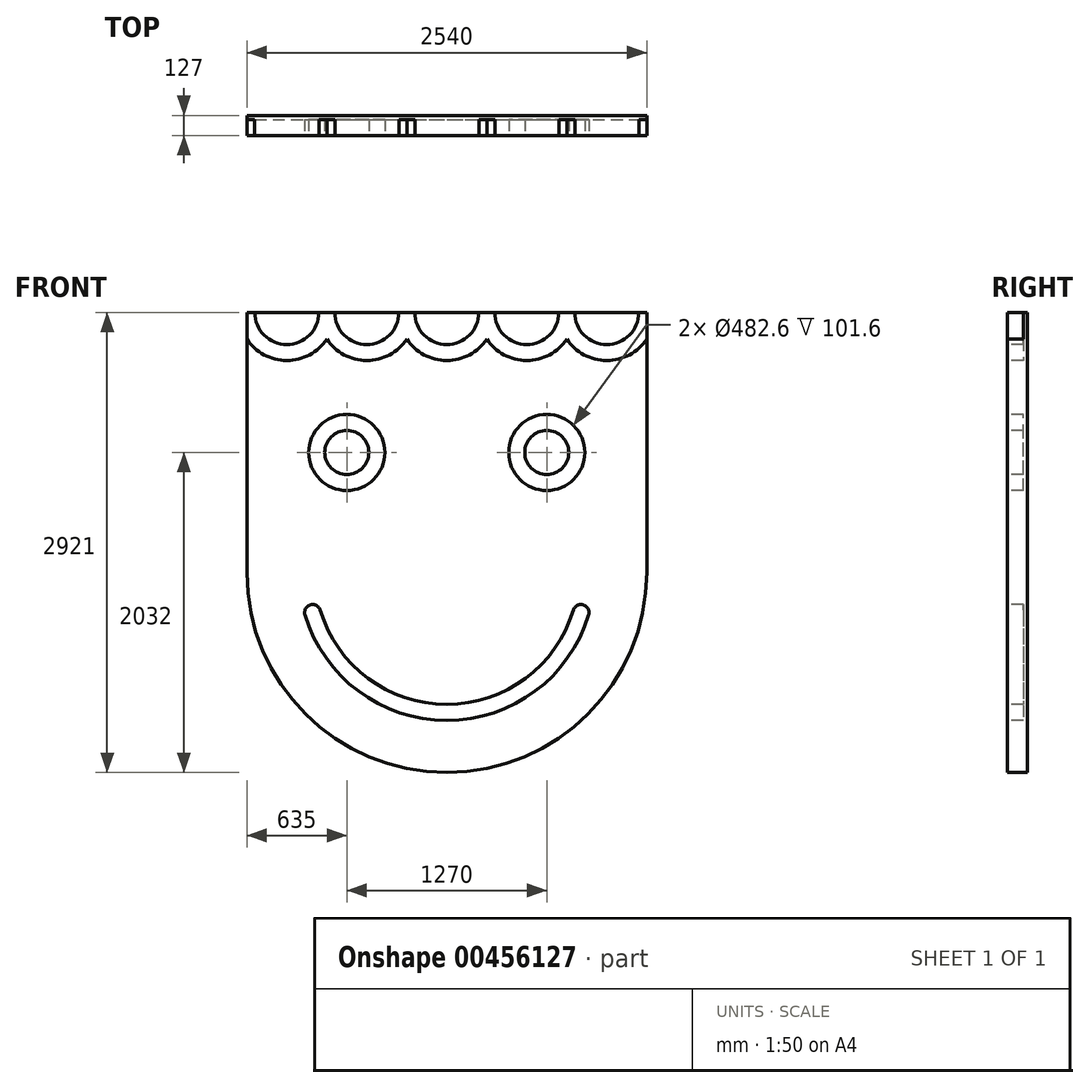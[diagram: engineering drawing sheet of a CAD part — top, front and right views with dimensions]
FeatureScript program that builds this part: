
annotation { "Feature Type Name" : "Feature", "Feature Type Description" : "" }
export const myFeature = defineFeature(function(context is Context, id is Id, definition is map)
    precondition{}
    {
        {
            var Q0;
            Q0=qCreatedBy(makeId("Front.planeOp"),FACE);
            var sketch = newSketch(context, id + "F0", { "sketchPlane" : qUnion([Q0])});
            skArc(sketch, "E0", {"start": v(-1270, 0) * mm, "mid": v(0, -1270) * mm, "end": v(1270, 0) * mm});
            skLineSegment(sketch, "E1", {"start": v(-1270, 0) * mm, "end": v(-1270, 1651) * mm});
            skLineSegment(sketch, "E2", {"start": v(-1270, 1651) * mm, "end": v(1270, 1651) * mm});
            skLineSegment(sketch, "E3", {"start": v(1270, 1651) * mm, "end": v(1270, 0) * mm});
            skSolve(sketch);
        }
        {
            var Q0;
            Q0 = qSketchRegion(id + "F0", true);
            extrude(context, id + "F1", {"entities" : qUnion([Q0]), "depth" : 127 * mm});
        }
        {
            var Q0;
            Q0=makeQuery(id+"F1.opExtrude","CAP_FACE",FACE,{"disambiguationData":[OSD([sQuery(id+"F0.wireOp",EDGE,"E0"),sQuery(id+"F0.wireOp",EDGE,"E1"),sQuery(id+"F0.wireOp",EDGE,"E2"),sQuery(id+"F0.wireOp",EDGE,"E3")])],"isStart":false});
            var sketch = newSketch(context, id + "F2", { "sketchPlane" : qUnion([Q0])});
            skArc(sketch, "E4", {"start": v(-851.94, -254) * mm, "mid": v(0, -889) * mm, "end": v(851.94, -254) * mm, "construction": true});
            skLineSegment(sketch, "E5", {"start": v(-1346.86, 0) * mm, "end": v(1410.17, 0) * mm, "construction": true});
            skCircle(sketch, "E6", {"center": v(-635, 762) * mm, "radius": 190.5 * mm, "construction": true});
            skCircle(sketch, "E7", {"center": v(635, 762) * mm, "radius": 190.5 * mm, "construction": true});
            skLineSegment(sketch, "E8", {"start": v(0, 0) * mm, "end": v(0, 1870.82) * mm, "construction": true});
            skArc(sketch, "E9", {"start": v(-1270, 1651) * mm, "mid": v(-1016, 1397) * mm, "end": v(-762, 1651) * mm, "construction": true});
            skArc(sketch, "E10", {"start": v(-762, 1651) * mm, "mid": v(-508, 1397) * mm, "end": v(-254, 1651) * mm, "construction": true});
            skArc(sketch, "E11", {"start": v(-254, 1651) * mm, "mid": v(0, 1397) * mm, "end": v(254, 1651) * mm, "construction": true});
            skArc(sketch, "E12", {"start": v(254, 1651) * mm, "mid": v(508, 1397) * mm, "end": v(762, 1651) * mm, "construction": true});
            skArc(sketch, "E13", {"start": v(762, 1651) * mm, "mid": v(1016, 1397) * mm, "end": v(1270, 1651) * mm, "construction": true});
            skArc(sketch, "E14.0.startCap", {"start": v(-1320.8, 1651) * mm, "mid": v(-1270, 1701.8) * mm, "end": v(-1219.2, 1651) * mm});
            skArc(sketch, "E14.0.endCap", {"start": v(-812.8, 1651) * mm, "mid": v(-762, 1701.8) * mm, "end": v(-711.2, 1651) * mm});
            skArc(sketch, "E14.0.left", {"start": v(-1219.2, 1651) * mm, "mid": v(-1016, 1447.8) * mm, "end": v(-812.8, 1651) * mm});
            skArc(sketch, "E14.0.right", {"start": v(-1320.8, 1651) * mm, "mid": v(-1016, 1346.2) * mm, "end": v(-711.2, 1651) * mm});
            skArc(sketch, "E14.1.startCap", {"start": v(-812.8, 1651) * mm, "mid": v(-762, 1701.8) * mm, "end": v(-711.2, 1651) * mm});
            skArc(sketch, "E14.1.endCap", {"start": v(-304.8, 1651) * mm, "mid": v(-254, 1701.8) * mm, "end": v(-203.2, 1651) * mm});
            skArc(sketch, "E14.1.left", {"start": v(-711.2, 1651) * mm, "mid": v(-508, 1447.8) * mm, "end": v(-304.8, 1651) * mm});
            skArc(sketch, "E14.1.right", {"start": v(-812.8, 1651) * mm, "mid": v(-508, 1346.2) * mm, "end": v(-203.2, 1651) * mm});
            skArc(sketch, "E14.2.startCap", {"start": v(-304.8, 1651) * mm, "mid": v(-254, 1701.8) * mm, "end": v(-203.2, 1651) * mm});
            skArc(sketch, "E14.2.endCap", {"start": v(203.2, 1651) * mm, "mid": v(254, 1701.8) * mm, "end": v(304.8, 1651) * mm});
            skArc(sketch, "E14.2.left", {"start": v(-203.2, 1651) * mm, "mid": v(0, 1447.8) * mm, "end": v(203.2, 1651) * mm});
            skArc(sketch, "E14.2.right", {"start": v(-304.8, 1651) * mm, "mid": v(0, 1346.2) * mm, "end": v(304.8, 1651) * mm});
            skArc(sketch, "E14.3.startCap", {"start": v(203.2, 1651) * mm, "mid": v(254, 1701.8) * mm, "end": v(304.8, 1651) * mm});
            skArc(sketch, "E14.3.endCap", {"start": v(711.2, 1651) * mm, "mid": v(762, 1701.8) * mm, "end": v(812.8, 1651) * mm});
            skArc(sketch, "E14.3.left", {"start": v(304.8, 1651) * mm, "mid": v(508, 1447.8) * mm, "end": v(711.2, 1651) * mm});
            skArc(sketch, "E14.3.right", {"start": v(203.2, 1651) * mm, "mid": v(508, 1346.2) * mm, "end": v(812.8, 1651) * mm});
            skArc(sketch, "E14.4.startCap", {"start": v(711.2, 1651) * mm, "mid": v(762, 1701.8) * mm, "end": v(812.8, 1651) * mm});
            skArc(sketch, "E14.4.endCap", {"start": v(1219.2, 1651) * mm, "mid": v(1270, 1701.8) * mm, "end": v(1320.8, 1651) * mm});
            skArc(sketch, "E14.4.left", {"start": v(812.8, 1651) * mm, "mid": v(1016, 1447.8) * mm, "end": v(1219.2, 1651) * mm});
            skArc(sketch, "E14.4.right", {"start": v(711.2, 1651) * mm, "mid": v(1016, 1346.2) * mm, "end": v(1320.8, 1651) * mm});
            skArc(sketch, "E14.5.startCap", {"start": v(-900.62, -268.51) * mm, "mid": v(-866.46, -205.32) * mm, "end": v(-803.26, -239.49) * mm});
            skArc(sketch, "E14.5.endCap", {"start": v(803.26, -239.49) * mm, "mid": v(866.46, -205.32) * mm, "end": v(900.62, -268.51) * mm});
            skArc(sketch, "E14.5.left", {"start": v(-803.26, -239.49) * mm, "mid": v(0, -838.2) * mm, "end": v(803.26, -239.49) * mm});
            skArc(sketch, "E14.5.right", {"start": v(-900.62, -268.51) * mm, "mid": v(0, -939.8) * mm, "end": v(900.62, -268.51) * mm});
            skArc(sketch, "E15.1.endCap", {"start": v(-304.8, 1651) * mm, "mid": v(-254, 1701.8) * mm, "end": v(-203.2, 1651) * mm, "construction": true});
            skArc(sketch, "E15.3.startCap", {"start": v(203.2, 1651) * mm, "mid": v(254, 1701.8) * mm, "end": v(304.8, 1651) * mm, "construction": true});
            skArc(sketch, "E15.3.endCap", {"start": v(711.2, 1651) * mm, "mid": v(762, 1701.8) * mm, "end": v(812.8, 1651) * mm, "construction": true});
            skCircle(sketch, "E16.0", {"center": v(-635, 762) * mm, "radius": 241.3 * mm});
            skCircle(sketch, "E17", {"center": v(635, 762) * mm, "radius": 241.3 * mm});
            skCircle(sketch, "E18", {"center": v(-635, 762) * mm, "radius": 139.7 * mm});
            skCircle(sketch, "E19", {"center": v(635, 762) * mm, "radius": 139.7 * mm});
            skSolve(sketch);
        }
        {
            var Q0;
            Q0 = qSketchRegion(id + "F2", true);
            extrude(context, id + "F3", {"entities" : qUnion([Q0]), "operationType" : NewBodyOperationType.REMOVE, "oppositeDirection" : true, "depth" : 101.6 * mm});
        }
        {
            var Q0;
            Q0=makeQuery(id+"F3.boolean.opBoolean","COPY",FACE,{"derivedFrom":makeQuery(id+"F3.opExtrude","CAP_FACE",FACE,{"disambiguationData":[OSD([sQuery(id+"F2.wireOp",EDGE,"E16.0")])],"isStart":false})});
            var sketch = newSketch(context, id + "F4", { "sketchPlane" : qUnion([Q0])});
            skCircle(sketch, "E20", {"center": v(-635, 762) * mm, "radius": 139.7 * mm});
            skSolve(sketch);
        }
        {
            var Q0;
            Q0=makeQuery(id+"F4.imprint","IMPRINT",FACE,{"disambiguationData":[TD([[makeQuery(id+"F4.imprint","IMPRINT",EDGE,{"derivedFrom":sQuery(id+"F4.wireOp",EDGE,"E20")}),1.0]])]});
            extrude(context, id + "F5", {"entities" : qUnion([Q0]), "operationType" : NewBodyOperationType.ADD, "depth" : 101.6 * mm});
        }
    });
